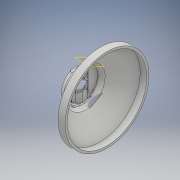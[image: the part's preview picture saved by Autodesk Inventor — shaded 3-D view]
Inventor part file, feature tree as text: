
AUTODESK INVENTOR PART (.ipt)
format: ipt  version: 2018 (Build 220112000, 112)  size: 2,707,968 bytes
history: native  units: mm
features: sketch x69, extrude x62, fillet x23, revolve x2, plane x2, mirror x1
ambient origin geometry x8: Origin, YZ Plane, XZ Plane, XY Plane, X Axis, Y Axis, Z Axis, Center Point
bodies: Solid1 (feature_tree)
feature tree (159):
  extrude  "Extrusion1"  TaperAngle=0.0deg  [1 undecoded]
  extrude  "Extrusion2"  Depth=10.0mm TaperAngle=0.0deg
  extrude  "Extrusion3"  Depth=10.0mm
  extrude  "Extrusion4"  TaperAngle=0.0deg  [1 undecoded]
  extrude  "Extrusion5"  Depth=10.0mm TaperAngle=0.0deg
  sketch  "Sketch6"  dims[d19=10.0mm d20=0.0mm d21=40.0mm]
  extrude  "Extrusion6"  Depth=10.0mm
  extrude  "Extrusion7"  Depth=11.0mm TaperAngle=0.0deg
  extrude  "Extrusion8"  Depth=32.0mm TaperAngle=0.0deg
  extrude  "Extrusion9"  Depth=32.0mm TaperAngle=0.0deg
  extrude  "Extrusion10"  Depth=10.0mm TaperAngle=0.0deg
  extrude  "Extrusion11"  Depth=10.0mm TaperAngle=0.0deg
  extrude  "Extrusion12"  TaperAngle=0.0deg  [1 undecoded]
  extrude  "Extrusion14"  Depth=48.3mm
  extrude  "Extrusion15"  TaperAngle=0.0deg  [1 undecoded]
  extrude  "Extrusion16"  Depth=10.0mm TaperAngle=0.0deg
  extrude  "Extrusion17"  Depth=11.63mm TaperAngle=0.0deg
  sketch  "Sketch21"  dims[d83=0.0mm d84=0.0mm d85=0.0mm d86=0.0mm]
  extrude  "Extrusion19"  Depth=11.63mm TaperAngle=0.0deg
  extrude  "Extrusion20"  TaperAngle=0.0deg  [1 undecoded]
  extrude  "Extrusion21"  Depth=10.0mm TaperAngle=0.0deg
  extrude  "Extrusion22"  TaperAngle=0.0deg  [1 undecoded]
  extrude  "Extrusion23"  Depth=2.86mm TaperAngle=0.0deg
  extrude  "Extrusion24"  Depth=2.01mm
  extrude  "Extrusion25"  Depth=10.0mm TaperAngle=0.0deg
  sketch  "Sketch33"  dims[d115=7.8mm d116=0.0mm d117=0.0mm d118=0.0mm]
  extrude  "Extrusion26"  Depth=10.0mm TaperAngle=0.0deg
  extrude  "Extrusion27"  TaperAngle=0.0deg  [1 undecoded]
  extrude  "Extrusion28"  Depth=22.0mm TaperAngle=0.0deg
  extrude  "Extrusion29"  Depth=17.0mm TaperAngle=0.0deg
  extrude  "Extrusion30"  Depth=2.0mm
  extrude  "Extrusion31"  Depth=6.95mm TaperAngle=0.0deg
  extrude  "Extrusion32"  Depth=18.0mm TaperAngle=0.0deg
  extrude  "Extrusion33"  Depth=1.02mm
  sketch  "Sketch42"  dims[d151=2.0mm d152=2.0mm]
  extrude  "Extrusion34"  Depth=7.72mm TaperAngle=0.0deg
  extrude  "Extrusion36"  Depth=2.0mm
  extrude  "Extrusion37"  Depth=2.0mm
  revolve  "Revolution3"  [1 undecoded]
  extrude  "Extrusion38"  Depth=2.0mm
  extrude  "Extrusion39"  Depth=10.0mm TaperAngle=0.0deg
  fillet  "Fillet1"  Radius=7.83mm
  fillet  "Fillet2"  Radius=20.0mm
  sketch  "Sketch51"  dims[d171=2.0mm d172=2.0mm]
  extrude  "Extrusion41"  Depth=6.4mm TaperAngle=0.0deg
  mirror  "Mirror1"
  extrude  "Extrusion42"  Depth=2.0mm
  sketch  "Sketch54"  dims[d181=2.0mm d182=2.0mm]
  sketch  "Sketch55"  dims[d183=2.0mm d184=2.0mm]
  sketch  "Sketch56"  dims[d185=2.0mm d186=7.85mm d187=0.0mm]
  extrude  "Extrusion44"  Depth=2.0mm
  extrude  "Extrusion45"  Depth=2.0mm
  extrude  "Extrusion46"  TaperAngle=90.0deg  [1 undecoded]
  extrude  "Extrusion47"  Depth=2.0mm
  plane  "Work Plane2"
  extrude  "Extrusion48"  Depth=2.0mm
  extrude  "Extrusion49"  Depth=7.85mm TaperAngle=0.0deg
  plane  "Work Plane5"
  extrude  "Extrusion50"  Depth=18.45mm TaperAngle=0.0deg
  extrude  "Extrusion51"  [1 undecoded]
  fillet  "Fillet3"  [1 undecoded]
  fillet  "Fillet4"  [1 undecoded]
  extrude  "Extrusion52"  [1 undecoded]
  extrude  "Extrusion53"  [1 undecoded]
  extrude  "Extrusion54"  [1 undecoded]
  extrude  "Extrusion55"  [1 undecoded]
  fillet  "Fillet5"  [1 undecoded]
  extrude  "Extrusion57"  [1 undecoded]
  extrude  "Extrusion58"  [1 undecoded]
  extrude  "Extrusion59"  [1 undecoded]
  fillet  "Fillet7"  [1 undecoded]
  fillet  "Fillet8"  [1 undecoded]
  fillet  "Fillet9"  [1 undecoded]
  fillet  "Fillet10"  [1 undecoded]
  fillet  "Fillet11"  [1 undecoded]
  fillet  "Fillet12"  [1 undecoded]
  fillet  "Fillet13"  [1 undecoded]
  fillet  "Fillet14"  [1 undecoded]
  extrude  "Extrusion60"  [1 undecoded]
  extrude  "Extrusion61"  [1 undecoded]
  extrude  "Extrusion62"  [1 undecoded]
  extrude  "Extrusion63"  [1 undecoded]
  extrude  "Extrusion64"  [1 undecoded]
  extrude  "Extrusion65"  [1 undecoded]
  fillet  "Fillet15"  [1 undecoded]
  fillet  "Fillet16"  [1 undecoded]
  fillet  "Fillet17"  [1 undecoded]
  fillet  "Fillet18"  [1 undecoded]
  fillet  "Fillet19"  [1 undecoded]
  revolve  "Revolution4"  [1 undecoded]
  fillet  "Fillet20"  [1 undecoded]
  fillet  "Fillet21"  [1 undecoded]
  fillet  "Fillet22"  [1 undecoded]
  fillet  "Fillet23"  [1 undecoded]
  fillet  "Fillet24"  [1 undecoded]
  extrude  "Extrusion66"  [1 undecoded]
  extrude  "Extrusion67"  [1 undecoded]
  extrude  "Extrusion68"  [1 undecoded]
  sketch  "Sketch1"  dims[d0=10.0mm d1=0.0mm d2=0.0mm d3=0.0mm]
  sketch  "Sketch2"  dims[d4=0.0mm d5=0.0mm d6=10.0mm d7=0.0mm]
  sketch  "Sketch3"  dims[d8=10.0mm d9=0.0mm d10=50.0mm]
  sketch  "Sketch4"  dims[d11=10.0mm d12=0.0mm d13=0.0mm d14=0.0mm]
  sketch  "Sketch5"  dims[d15=0.0mm d16=0.0mm d17=10.0mm d18=0.0mm]
  sketch  "Sketch7"  dims[d22=38.0mm d23=11.0mm d24=0.0mm]
  sketch  "Sketch8"  dims[d25=9.5mm d26=0.0mm d33=32.0mm d34=0.0mm]
  sketch  "Sketch9"  dims[d37=32.0mm d38=0.0mm d39=32.0mm d40=0.0mm]
  sketch  "Sketch10"  dims[d41=32.0mm d42=0.0mm d45=10.0mm d46=0.0mm]
  sketch  "Sketch11"  dims[d47=10.0mm d48=0.0mm d49=10.0mm d50=0.0mm]
  sketch  "Sketch12"  dims[d51=0.0mm d52=0.0mm d53=0.0mm d54=0.0mm]
  sketch  "Sketch13"  dims[d65=46.0mm d66=48.3mm]
  sketch  "Sketch16"  dims[d67=9.0mm d68=0.0mm d69=0.0mm d70=0.0mm]
  sketch  "Sketch18"  dims[d71=0.0mm d72=0.0mm d73=10.0mm d74=0.0mm]
  sketch  "Sketch19"  dims[d75=5.0mm d76=0.0mm d77=11.63mm d78=0.0mm]
  sketch  "Sketch20"  dims[d79=11.63mm d80=0.0mm d81=11.63mm d82=0.0mm]
  sketch  "Sketch22"  dims[d87=30.0mm d88=10.0mm d89=0.0mm]
  sketch  "Sketch23"  dims[d92=10.0mm d93=0.0mm d94=0.0mm d95=0.0mm]
  sketch  "Sketch24"  dims[d96=135.0deg d99=2.86mm d100=0.0mm]
  sketch  "Sketch25"  dims[d101=0.0mm d102=0.0mm d105=2.01mm]
  sketch  "Sketch31"  dims[d106=2.22mm d107=10.0mm d108=0.0mm]
  sketch  "Sketch32"  dims[d109=10.0mm d110=0.0mm d113=7.8mm d114=0.0mm]
  sketch  "Sketch34"  dims[d119=16.0mm d120=0.0mm d121=22.0mm d122=0.0mm]
  sketch  "Sketch35"  dims[d123=22.0mm d124=0.0mm d126=17.0mm d127=0.0mm]
  sketch  "Sketch36"  dims[d128=17.0mm d129=0.0mm d130=2.0mm]
  sketch  "Sketch37"  dims[d131=2.0mm d132=6.95mm d133=0.0mm]
  sketch  "Sketch38"  dims[d134=6.95mm d135=0.0mm d136=18.0mm d137=0.0mm]
  sketch  "Sketch39"  dims[d138=16.0mm d139=0.0mm d140=1.02mm]
  sketch  "Sketch40"  dims[d143=15.5mm d144=0.0mm d146=7.72mm d147=0.0mm]
  sketch  "Sketch41"  dims[d148=17.0mm d149=0.0mm d150=2.0mm]
  sketch  "Sketch43"  dims[d153=2.0mm d154=2.0mm]
  sketch  "Sketch45"  dims[d155=2.0mm d156=2.0mm]
  sketch  "Sketch47"  dims[d157=2.0mm d158=10.0mm d159=0.0mm d160=7.83mm d161=0.0mm d162=20.0mm d163=0.0mm]
  sketch  "Sketch48"  dims[d164=0.0mm d165=0.0mm d166=6.4mm d167=0.0mm]
  sketch  "Sketch49"  dims[d168=6.14mm d169=0.0mm d170=2.0mm]
  sketch  "Sketch52"  dims[d173=2.0mm d174=2.0mm]
  sketch  "Sketch53"  dims[d175=1.5mm d176=1.5mm d177=3.0mm d178=10.0mm d180=90.0deg]
  sketch  "Sketch57"  dims[d188=18.45mm d189=0.0mm d190=18.45mm d191=0.0mm]
  sketch  "Sketch60"
  sketch  "Sketch61"
  sketch  "Sketch62"
  sketch  "Sketch63"
  sketch  "Sketch65"
  sketch  "Sketch66"
  sketch  "Sketch67"
  sketch  "Sketch68"
  sketch  "Sketch69"
  sketch  "Sketch70"
  sketch  "Sketch72"
  sketch  "Sketch73"
  sketch  "Sketch74"
  sketch  "Sketch75"
  sketch  "Sketch76"
  sketch  "Sketch78"
  sketch  "Sketch80"
  sketch  "Sketch81"
  sketch  "Sketch82"
  sketch  "Sketch83"
  sketch  "Sketch84"
  sketch  "Sketch85"
  sketch  "Sketch86"
note: 48 required parameter values undecoded (feature->parameter linkage not recoverable at this tier; creation-order binding heuristic only, values carry confidence <= 0.55)